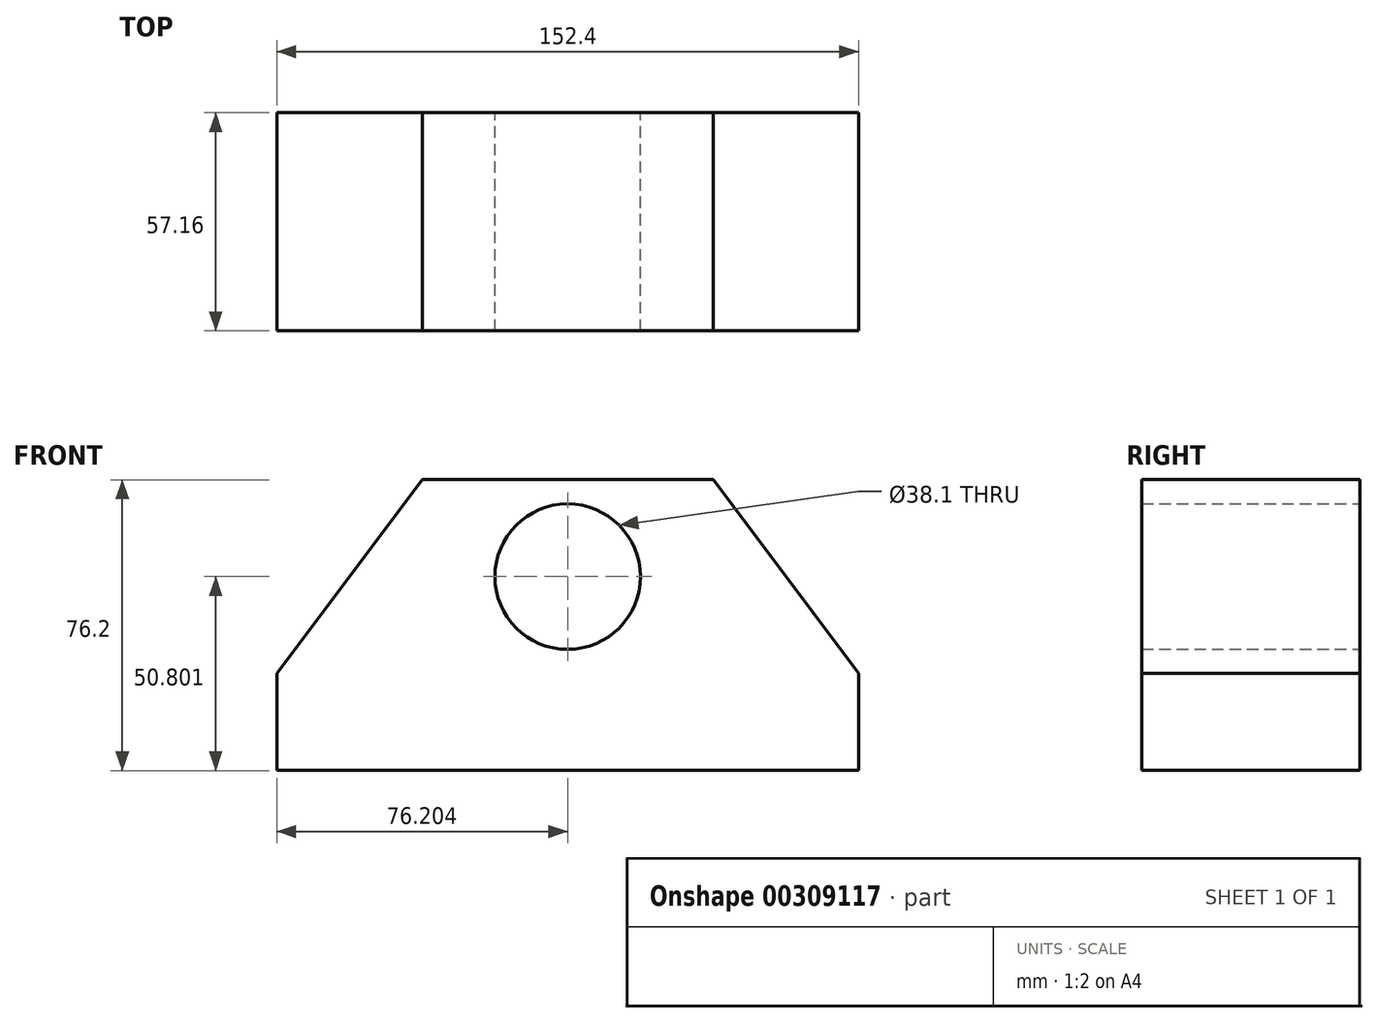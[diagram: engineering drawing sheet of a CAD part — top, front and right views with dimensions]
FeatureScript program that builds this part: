
annotation { "Feature Type Name" : "Feature", "Feature Type Description" : "" }
export const myFeature = defineFeature(function(context is Context, id is Id, definition is map)
    precondition{}
    {
        {
            var Q0;
            Q0=qCreatedBy(makeId("Front.planeOp"),FACE);
            var sketch = newSketch(context, id + "F0", { "sketchPlane" : qUnion([Q0])});
            skLineSegment(sketch, "E0", {"start": v(-20.55, 58.53) * mm, "end": v(55.65, 58.53) * mm});
            skLineSegment(sketch, "E1", {"start": v(55.65, 58.53) * mm, "end": v(93.75, 7.73) * mm});
            skLineSegment(sketch, "E2", {"start": v(93.75, 7.73) * mm, "end": v(93.75, -17.67) * mm});
            skLineSegment(sketch, "E3", {"start": v(-20.55, 58.53) * mm, "end": v(-58.65, 7.73) * mm});
            skLineSegment(sketch, "E4", {"start": v(-58.65, 7.73) * mm, "end": v(-58.65, -17.67) * mm});
            skLineSegment(sketch, "E5", {"start": v(-58.65, -17.67) * mm, "end": v(93.75, -17.67) * mm});
            skPoint(sketch, "E6.centerSnap0", {"position": v(17.55, 58.53) * mm});
            skCircle(sketch, "E7", {"center": v(17.55, 33.13) * mm, "radius": 19.05 * mm});
            skSolve(sketch);
        }
        {
            var Q0;
            Q0 = qSketchRegion(id + "F0", true);
            extrude(context, id + "F1", {"entities" : qUnion([Q0]), "endBound" : BoundingType.SYMMETRIC, "depth" : 57.15 * mm});
        }
    });
